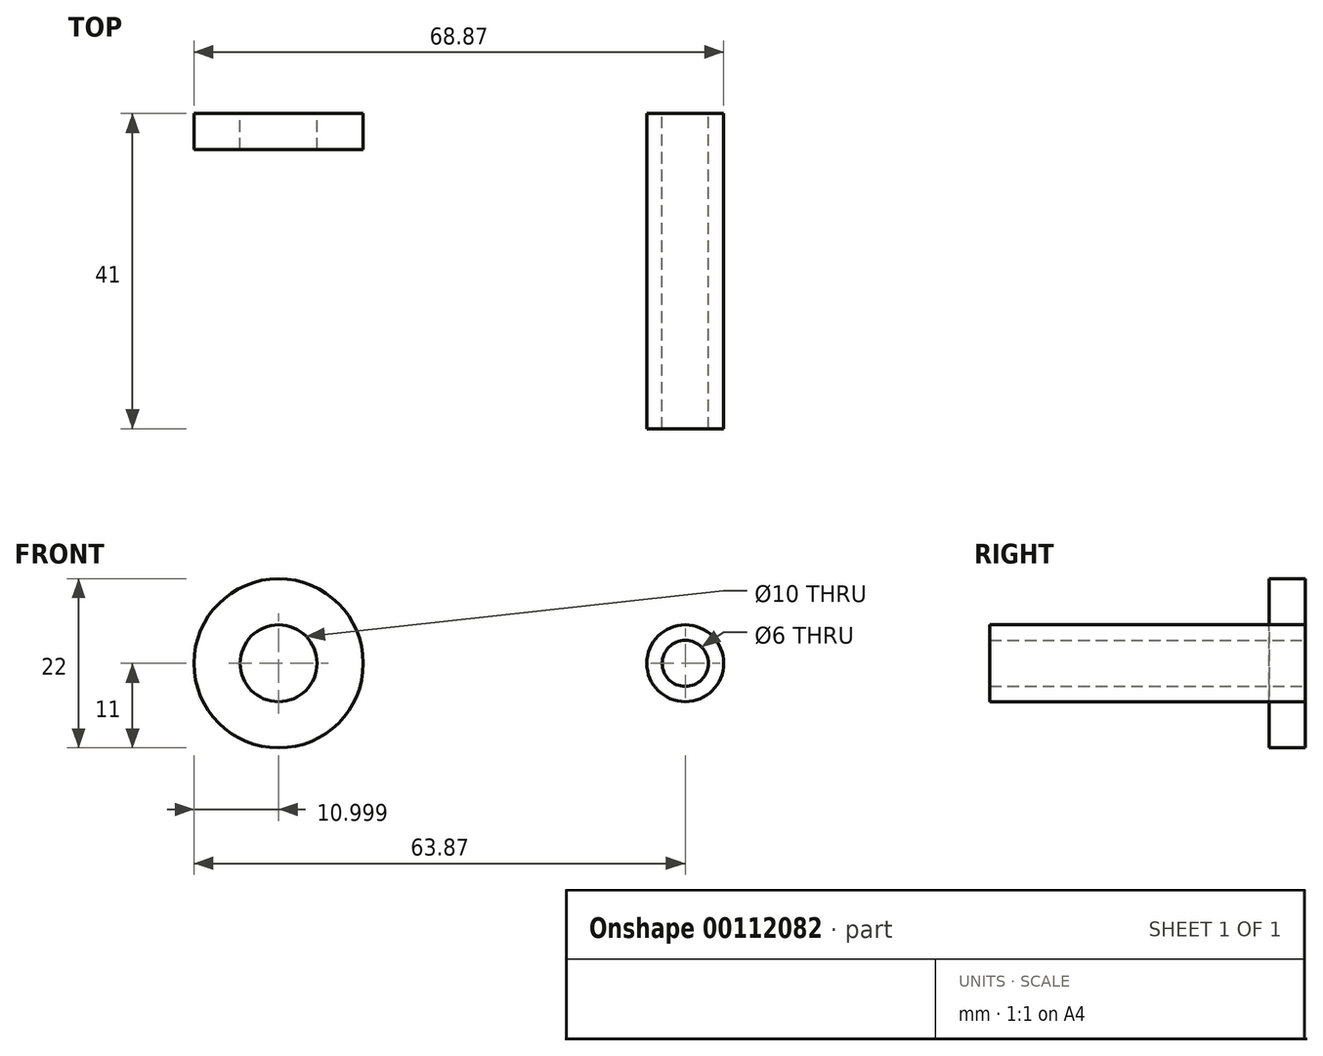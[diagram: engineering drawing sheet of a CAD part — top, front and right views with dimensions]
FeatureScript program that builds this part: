
annotation { "Feature Type Name" : "Feature", "Feature Type Description" : "" }
export const myFeature = defineFeature(function(context is Context, id is Id, definition is map)
    precondition{}
    {
        {
            var Q0;
            Q0=qCreatedBy(makeId("Front.planeOp"),FACE);
            var sketch = newSketch(context, id + "F0", { "sketchPlane" : qUnion([Q0])});
            skCircle(sketch, "E0", {"center": v(0, 0) * mm, "radius": 3 * mm});
            skCircle(sketch, "E1", {"center": v(0, 0) * mm, "radius": 5 * mm});
            skCircle(sketch, "E2", {"center": v(-52.87, 0) * mm, "radius": 5 * mm});
            skCircle(sketch, "E3", {"center": v(-52.87, 0) * mm, "radius": 11 * mm});
            skSolve(sketch);
        }
        {
            var Q0;
            Q0=makeQuery(id+"F0.imprint","IMPRINT",FACE,{"disambiguationData":[TD([[makeQuery(id+"F0.imprint","IMPRINT",EDGE,{"derivedFrom":sQuery(id+"F0.wireOp",EDGE,"E0")}),-1.0]])]});
            extrude(context, id + "F1", {"entities" : qUnion([Q0]), "depth" : 41 * mm});
        }
        {
            var Q0;
            Q0 = qSketchRegion(id + "F0", true);
            extrude(context, id + "F2", {"entities" : qUnion([Q0]), "operationType" : NewBodyOperationType.ADD, "depth" : 4.7 * mm});
        }
    });
